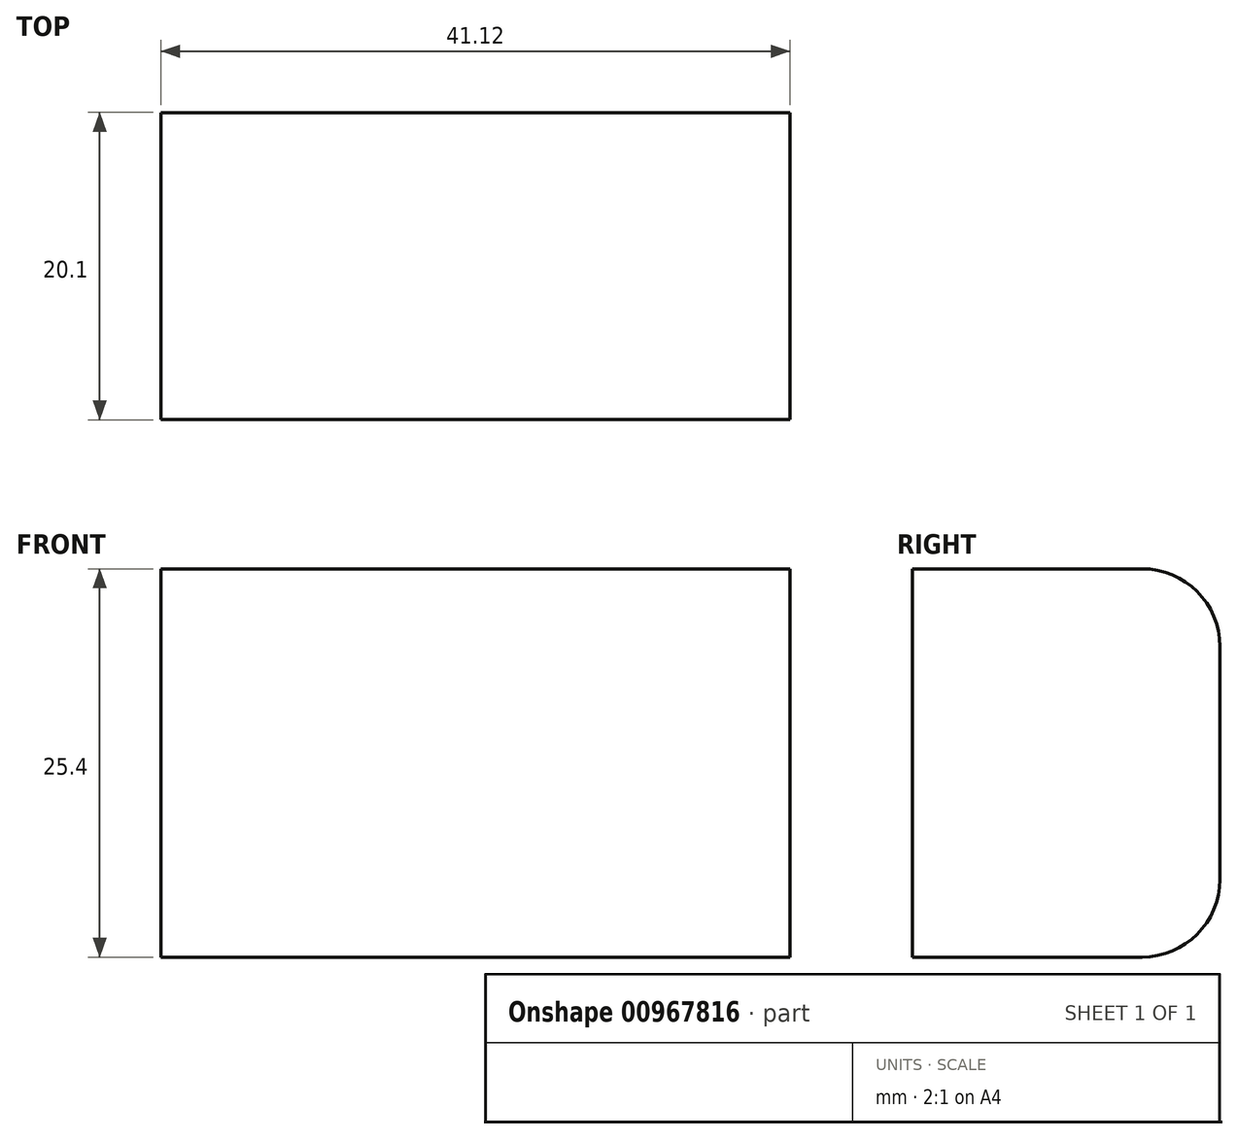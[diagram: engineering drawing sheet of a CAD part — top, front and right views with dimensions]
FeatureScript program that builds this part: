
annotation { "Feature Type Name" : "Feature", "Feature Type Description" : "" }
export const myFeature = defineFeature(function(context is Context, id is Id, definition is map)
    precondition{}
    {
        {
            var Q0;
            Q0=qCreatedBy(makeId("Top.planeOp"),FACE);
            var sketch = newSketch(context, id + "F0", { "sketchPlane" : qUnion([Q0])});
            skLineSegment(sketch, "E0.bottom", {"start": v(20.56, -10.05) * mm, "end": v(-20.56, -10.05) * mm});
            skLineSegment(sketch, "E0.top", {"start": v(20.56, 10.05) * mm, "end": v(-20.56, 10.05) * mm});
            skLineSegment(sketch, "E0.left", {"start": v(20.56, -10.05) * mm, "end": v(20.56, 10.05) * mm});
            skLineSegment(sketch, "E0.right", {"start": v(-20.56, -10.05) * mm, "end": v(-20.56, 10.05) * mm});
            skPoint(sketch, "E0.middle", {"position": v(0, 0) * mm});
            skSolve(sketch);
        }
        {
            var Q0;
            Q0 = qSketchRegion(id + "F0", true);
            extrude(context, id + "F1", {"entities" : qUnion([Q0]), "depth" : 25.4 * mm, "offsetDistance" : 25.4 * mm});
        }
        {
            var Q0;
            Q0=makeQuery(id+"F1.opExtrude","CAP_EDGE",EDGE,{"disambiguationData":[OSD([sQuery(id+"F0.wireOp",EDGE,"E0.top")])],"isStart":false});
            var Q1;
            Q1=makeQuery(id+"F1.opExtrude","CAP_EDGE",EDGE,{"disambiguationData":[OSD([sQuery(id+"F0.wireOp",EDGE,"E0.top")])],"isStart":true});
            fillet(context, id + "F2", {"entities" : qUnion([Q0, Q1]), "radius" : 5.08 * mm, "tangentPropagation" : true, "allowEdgeOverflow" : false});
        }
    });
